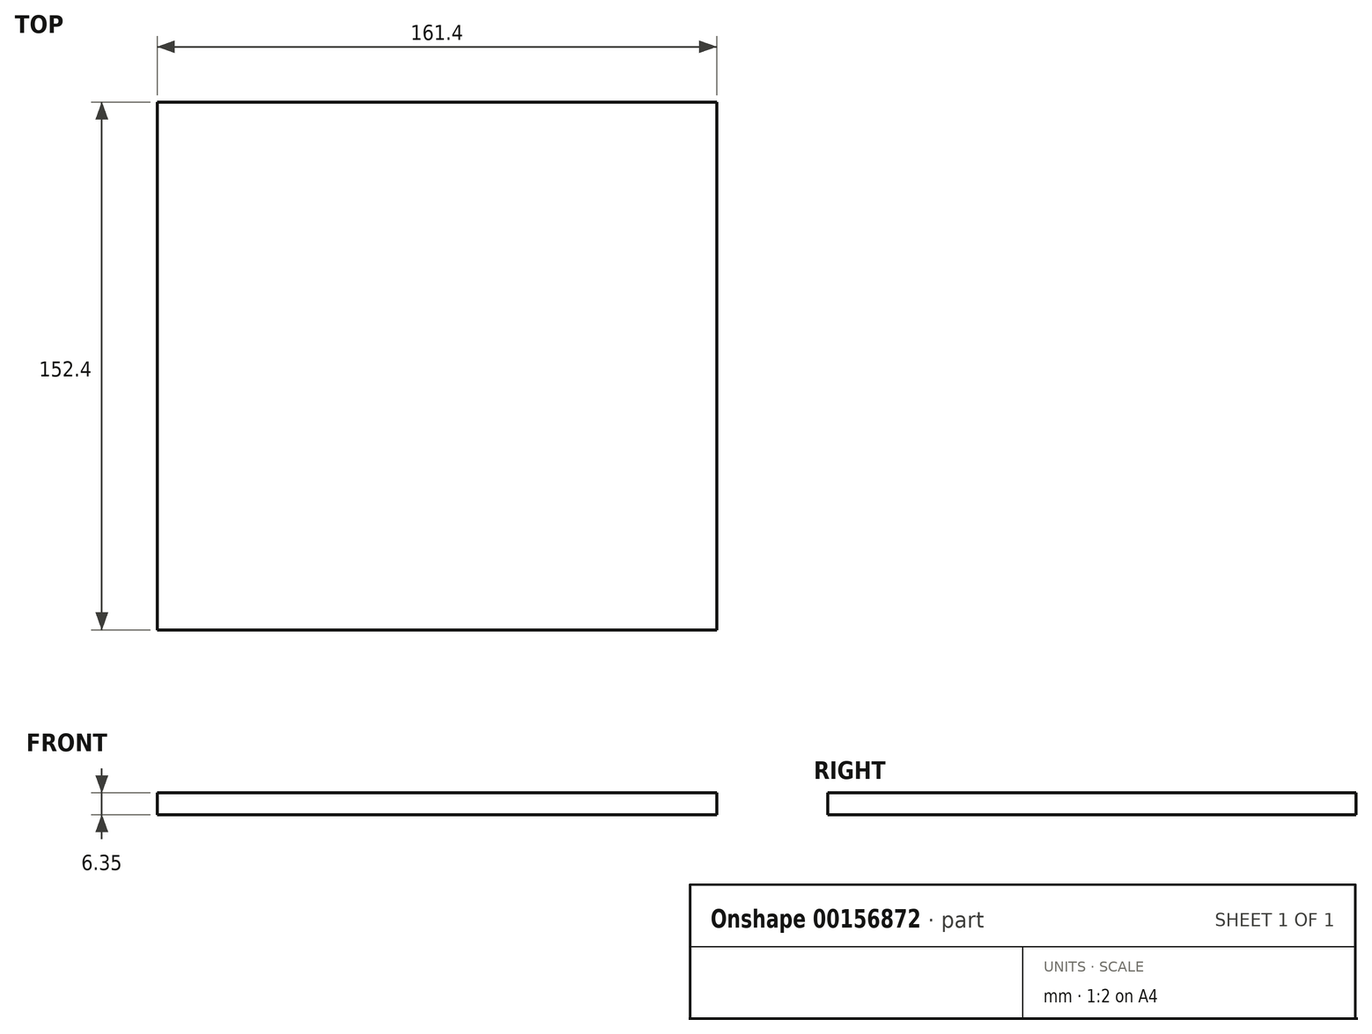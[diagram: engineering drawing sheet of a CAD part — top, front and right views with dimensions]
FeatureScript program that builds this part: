
annotation { "Feature Type Name" : "Feature", "Feature Type Description" : "" }
export const myFeature = defineFeature(function(context is Context, id is Id, definition is map)
    precondition{}
    {
        {
            var Q0;
            Q0=qCreatedBy(makeId("Top.planeOp"),FACE);
            var sketch = newSketch(context, id + "F0", { "sketchPlane" : qUnion([Q0])});
            skLineSegment(sketch, "E0.bottom", {"start": v(80.7, 76.2) * mm, "end": v(-80.7, 76.2) * mm});
            skLineSegment(sketch, "E0.top", {"start": v(80.7, -76.2) * mm, "end": v(-80.7, -76.2) * mm});
            skLineSegment(sketch, "E0.left", {"start": v(80.7, 76.2) * mm, "end": v(80.7, -76.2) * mm});
            skLineSegment(sketch, "E0.right", {"start": v(-80.7, 76.2) * mm, "end": v(-80.7, -76.2) * mm});
            skPoint(sketch, "E0.middle", {"position": v(0, 0) * mm});
            skSolve(sketch);
        }
        {
            var Q0;
            Q0 = qSketchRegion(id + "F0", true);
            extrude(context, id + "F1", {"entities" : qUnion([Q0]), "depth" : 6.35 * mm});
        }
    });
